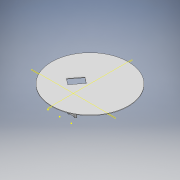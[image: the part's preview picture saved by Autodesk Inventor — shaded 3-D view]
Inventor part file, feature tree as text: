
AUTODESK INVENTOR PART (.ipt)
format: ipt  version: 2020 (Build 240168000, 168)  size: 201,728 bytes
history: native  units: mm
features: sketch x5, other x3, plane x2
ambient origin geometry x8: Origin, YZ Plane, XZ Plane, XY Plane, X Axis, Y Axis, Z Axis, Center Point
bodies: Solid1 (feature_tree)
feature tree (10):
  other  "Assembly1.iam"
  other  "GonjaKonstrukcija_v.1.0.ipt:1"
  other  "5DržačaLidara.ipt:1"
  plane  "Work Plane1"
  plane  "Work Plane2"
  sketch  "Sketch8"
  sketch  "Sketch8_1"  dims[d0=10.0mm]
  sketch  "Sketch8_2"
  sketch  "Sketch8_3"
  sketch  "Sketch8_4"
